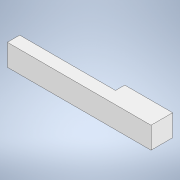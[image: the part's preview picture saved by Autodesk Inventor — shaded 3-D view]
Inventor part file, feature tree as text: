
AUTODESK INVENTOR PART (.ipt)
format: ipt  version: 2021 (Build 250183000, 183)  size: 95,232 bytes
history: native  units: in
note: dims shown in document units (in); Inventor stores cm internally (conversion verified against a paired STEP export)
features: extrude x1, sketch x1
ambient origin geometry x8: Origin, YZ Plane, XZ Plane, XY Plane, X Axis, Y Axis, Z Axis, Center Point
bodies: Solid1 (feature_tree)
feature tree (2):
  extrude  "Extrusion1"  Depth=5.8125in
  sketch  "Sketch1"  dims[d3=0.5in d4=5.8125in d5=0.875in d6=3.875in d7=0.875in d8=0.0in]
